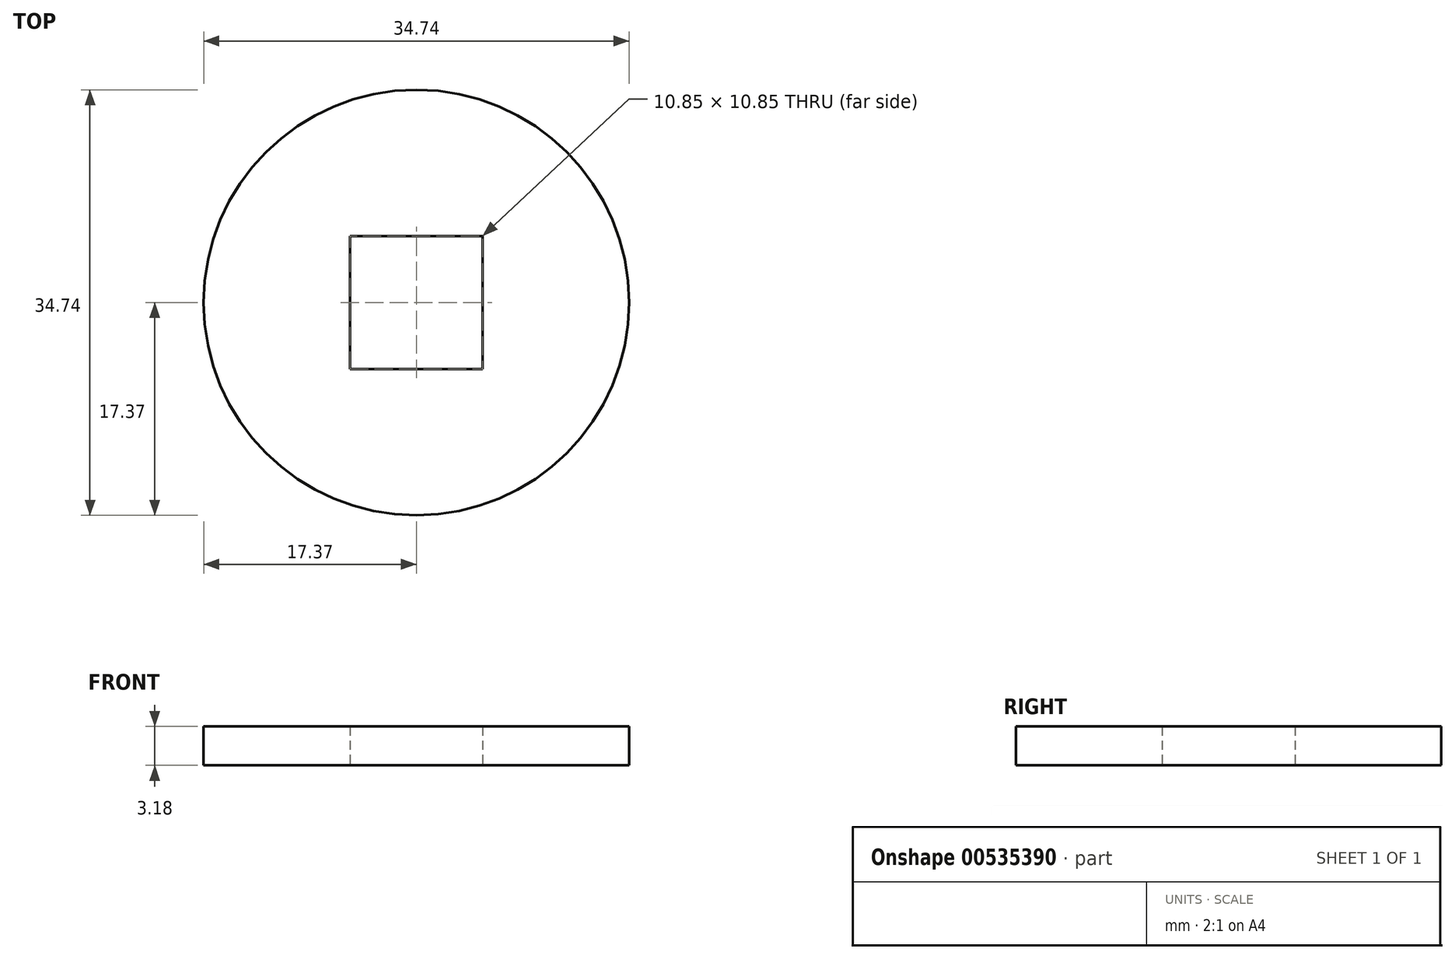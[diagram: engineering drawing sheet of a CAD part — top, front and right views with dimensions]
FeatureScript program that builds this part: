
annotation { "Feature Type Name" : "Feature", "Feature Type Description" : "" }
export const myFeature = defineFeature(function(context is Context, id is Id, definition is map)
    precondition{}
    {
        {
            var Q0;
            Q0=qCreatedBy(makeId("Top.planeOp"),FACE);
            var sketch = newSketch(context, id + "F0", { "sketchPlane" : qUnion([Q0])});
            skCircle(sketch, "E0", {"center": v(0, 0) * mm, "radius": 17.37 * mm});
            skLineSegment(sketch, "E1.bottom", {"start": v(5.42, 5.42) * mm, "end": v(-5.42, 5.42) * mm});
            skLineSegment(sketch, "E1.top", {"start": v(5.42, -5.42) * mm, "end": v(-5.42, -5.42) * mm});
            skLineSegment(sketch, "E1.left", {"start": v(5.42, 5.42) * mm, "end": v(5.42, -5.42) * mm});
            skLineSegment(sketch, "E1.right", {"start": v(-5.42, 5.42) * mm, "end": v(-5.42, -5.42) * mm});
            skSolve(sketch);
        }
        {
            var Q0;
            Q0=makeQuery(id+"F0.imprint","IMPRINT",FACE,{"disambiguationData":[TD([[makeQuery(id+"F0.imprint","IMPRINT",EDGE,{"derivedFrom":sQuery(id+"F0.wireOp",EDGE,"E0")}),1.0]])]});
            extrude(context, id + "F1", {"entities" : qUnion([Q0]), "depth" : 3.17 * mm, "offsetDistance" : 25 * mm});
        }
    });
